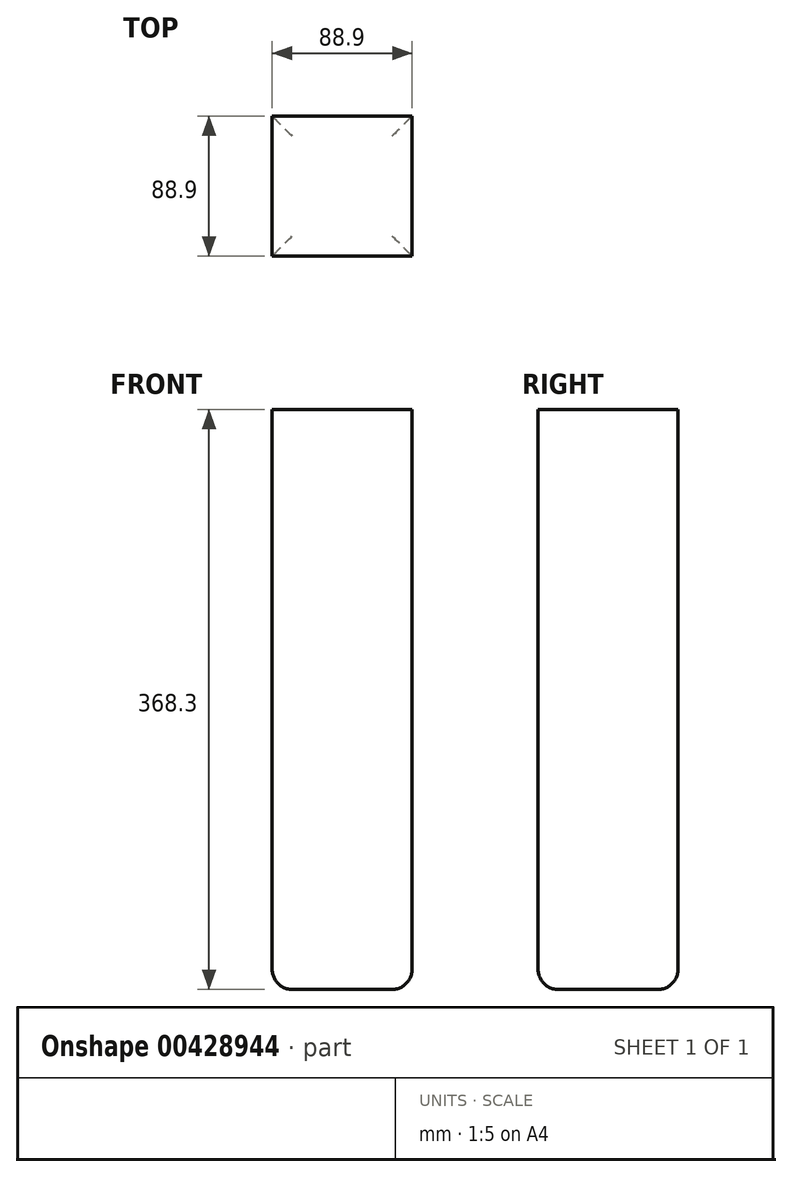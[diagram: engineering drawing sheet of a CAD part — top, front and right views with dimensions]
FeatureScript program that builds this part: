
annotation { "Feature Type Name" : "Feature", "Feature Type Description" : "" }
export const myFeature = defineFeature(function(context is Context, id is Id, definition is map)
    precondition{}
    {
        {
            var Q0;
            Q0=qCreatedBy(makeId("Top.planeOp"),FACE);
            var sketch = newSketch(context, id + "F0", { "sketchPlane" : qUnion([Q0])});
            skLineSegment(sketch, "E0.bottom", {"start": v(-106.57, 43.1) * mm, "end": v(-17.67, 43.1) * mm});
            skLineSegment(sketch, "E0.top", {"start": v(-106.57, -45.8) * mm, "end": v(-17.67, -45.8) * mm});
            skLineSegment(sketch, "E0.left", {"start": v(-106.57, 43.1) * mm, "end": v(-106.57, -45.8) * mm});
            skLineSegment(sketch, "E0.right", {"start": v(-17.67, 43.1) * mm, "end": v(-17.67, -45.8) * mm});
            skSolve(sketch);
        }
        {
            var Q0;
            Q0=makeQuery(id+"F0.imprint","IMPRINT",FACE,{"disambiguationData":[TD([[makeQuery(id+"F0.imprint","IMPRINT",EDGE,{"derivedFrom":sQuery(id+"F0.wireOp",EDGE,"E0.bottom")}),-1.0]])]});
            extrude(context, id + "F1", {"entities" : qUnion([Q0]), "depth" : 368.3 * mm});
        }
        {
            var Q0;
            Q0=makeQuery(id+"F1.opExtrude","CAP_EDGE",EDGE,{"disambiguationData":[OSD([sQuery(id+"F0.wireOp",EDGE,"E0.top")])],"isStart":true});
            var Q1;
            Q1=makeQuery(id+"F1.opExtrude","CAP_EDGE",EDGE,{"disambiguationData":[OSD([sQuery(id+"F0.wireOp",EDGE,"E0.right")])],"isStart":true});
            var Q2;
            Q2=makeQuery(id+"F1.opExtrude","CAP_EDGE",EDGE,{"disambiguationData":[OSD([sQuery(id+"F0.wireOp",EDGE,"E0.bottom")])],"isStart":true});
            var Q3;
            Q3=makeQuery(id+"F1.opExtrude","CAP_EDGE",EDGE,{"disambiguationData":[OSD([sQuery(id+"F0.wireOp",EDGE,"E0.left")])],"isStart":true});
            fillet(context, id + "F2", {"entities" : qUnion([Q0, Q1, Q2, Q3]), "radius" : 12.7 * mm, "tangentPropagation" : true, "allowEdgeOverflow" : false});
        }
    });
